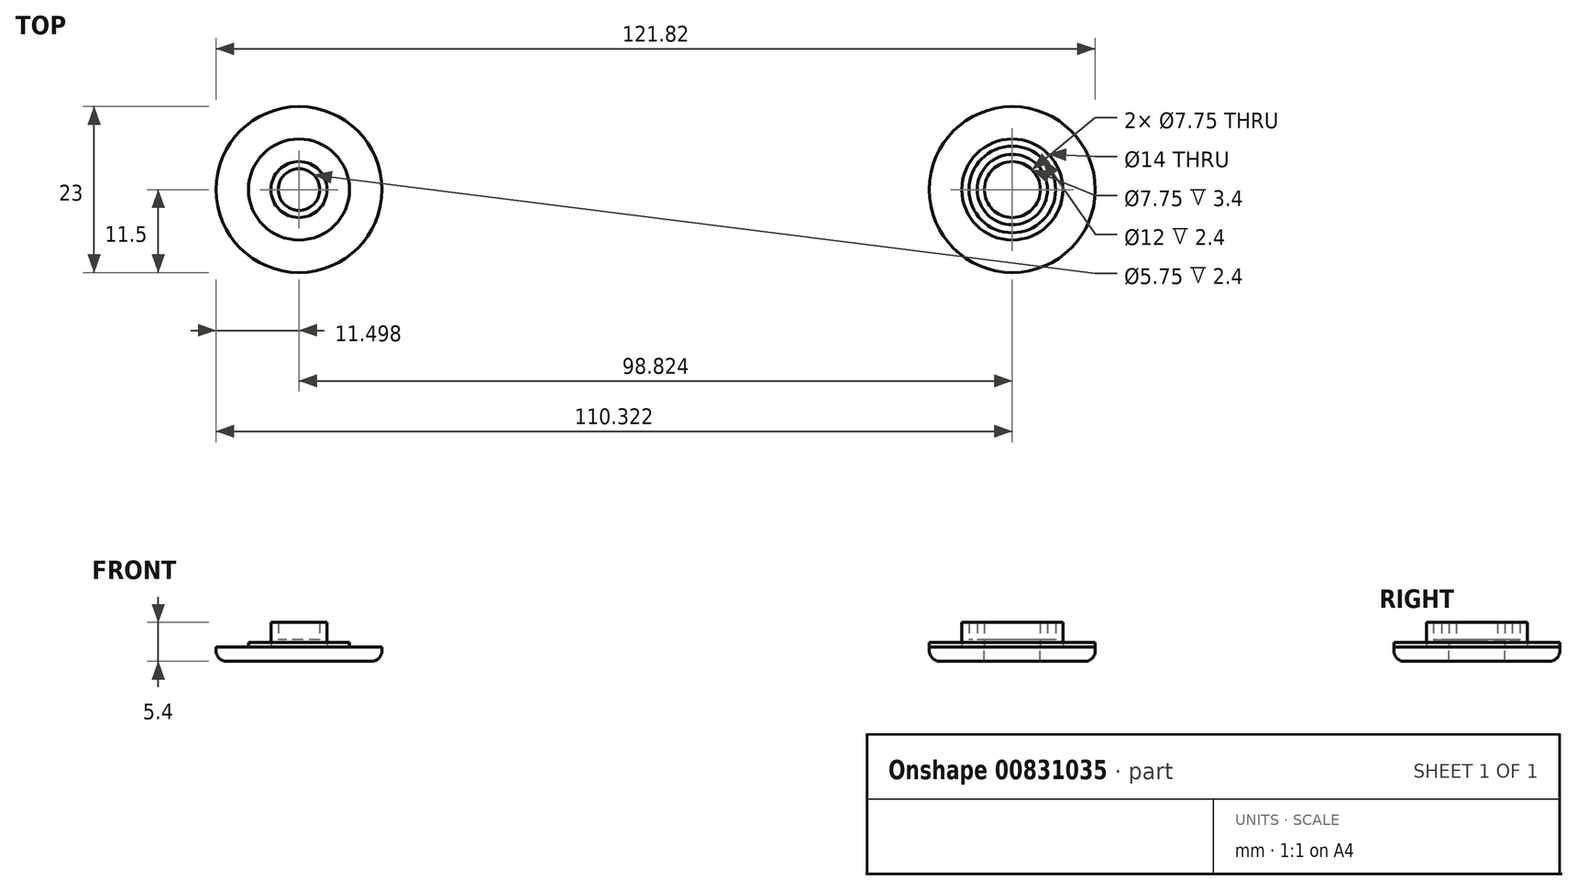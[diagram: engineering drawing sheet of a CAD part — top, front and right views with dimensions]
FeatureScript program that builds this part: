
annotation { "Feature Type Name" : "Feature", "Feature Type Description" : "" }
export const myFeature = defineFeature(function(context is Context, id is Id, definition is map)
    precondition{}
    {
        {
            var Q0;
            Q0=qCreatedBy(makeId("Top.planeOp"),FACE);
            var sketch = newSketch(context, id + "F0", { "sketchPlane" : qUnion([Q0])});
            skCircle(sketch, "E0", {"center": v(-49.41, 0) * mm, "radius": 3.88 * mm});
            skCircle(sketch, "E1", {"center": v(-49.41, 0) * mm, "radius": 7 * mm});
            skCircle(sketch, "E2", {"center": v(-49.41, 0) * mm, "radius": 11.5 * mm});
            skCircle(sketch, "E3.MirrorC", {"center": v(49.41, 0) * mm, "radius": 11.5 * mm});
            skCircle(sketch, "E4.MirrorC", {"center": v(49.41, 0) * mm, "radius": 7 * mm});
            skCircle(sketch, "E5.MirrorC", {"center": v(49.41, 0) * mm, "radius": 3.88 * mm});
            skSolve(sketch);
        }
        {
            var Q0;
            Q0=makeQuery(id+"F0.imprint","IMPRINT",FACE,{"disambiguationData":[TD([[makeQuery(id+"F0.imprint","IMPRINT",EDGE,{"derivedFrom":sQuery(id+"F0.wireOp",EDGE,"E0")}),1.0]])]});
            var Q1;
            Q1=makeQuery(id+"F0.imprint","IMPRINT",FACE,{"disambiguationData":[TD([[makeQuery(id+"F0.imprint","IMPRINT",EDGE,{"derivedFrom":sQuery(id+"F0.wireOp",EDGE,"E5.MirrorC")}),-1.0]])]});
            extrude(context, id + "F1", {"entities" : qUnion([Q0, Q1]), "depth" : 3.4 * mm, "offsetDistance" : 25 * mm});
        }
        {
            var Q0;
            Q0=makeQuery(id+"F0.imprint","IMPRINT",FACE,{"disambiguationData":[TD([[makeQuery(id+"F0.imprint","IMPRINT",EDGE,{"derivedFrom":sQuery(id+"F0.wireOp",EDGE,"E0")}),-1.0]])]});
            var Q1;
            Q1=makeQuery(id+"F0.imprint","IMPRINT",FACE,{"disambiguationData":[TD([[makeQuery(id+"F0.imprint","IMPRINT",EDGE,{"derivedFrom":sQuery(id+"F0.wireOp",EDGE,"E4.MirrorC")}),-1.0]])]});
            extrude(context, id + "F2", {"entities" : qUnion([Q0, Q1]), "depth" : 0.6 * mm, "offsetDistance" : 25 * mm});
        }
        {
            var Q0;
            Q0=makeQuery(id+"F0.imprint","IMPRINT",FACE,{"disambiguationData":[TD([[makeQuery(id+"F0.imprint","IMPRINT",EDGE,{"derivedFrom":sQuery(id+"F0.wireOp",EDGE,"E1")}),-1.0]])]});
            var Q1;
            Q1=makeQuery(id+"F0.imprint","IMPRINT",FACE,{"disambiguationData":[TD([[makeQuery(id+"F0.imprint","IMPRINT",EDGE,{"derivedFrom":sQuery(id+"F0.wireOp",EDGE,"E3.MirrorC")}),-1.0]])]});
            var Q2;
            Q2=makeQuery(id+"F0.imprint","IMPRINT",FACE,{"disambiguationData":[TD([[makeQuery(id+"F0.imprint","IMPRINT",EDGE,{"derivedFrom":sQuery(id+"F0.wireOp",EDGE,"E0")}),-1.0]])]});
            var Q3;
            Q3=makeQuery(id+"F0.imprint","IMPRINT",FACE,{"disambiguationData":[TD([[makeQuery(id+"F0.imprint","IMPRINT",EDGE,{"derivedFrom":sQuery(id+"F0.wireOp",EDGE,"E0")}),1.0]])]});
            var Q4;
            Q4=makeQuery(id+"F0.imprint","IMPRINT",FACE,{"disambiguationData":[TD([[makeQuery(id+"F0.imprint","IMPRINT",EDGE,{"derivedFrom":sQuery(id+"F0.wireOp",EDGE,"E5.MirrorC")}),-1.0]])]});
            var Q5;
            Q5=makeQuery(id+"F0.imprint","IMPRINT",FACE,{"disambiguationData":[TD([[makeQuery(id+"F0.imprint","IMPRINT",EDGE,{"derivedFrom":sQuery(id+"F0.wireOp",EDGE,"E4.MirrorC")}),-1.0]])]});
            extrude(context, id + "F3", {"entities" : qUnion([Q0, Q1, Q2, Q3, Q4, Q5]), "oppositeDirection" : true, "depth" : 2 * mm, "offsetDistance" : 25 * mm});
        }
        {
            var Q0;
            Q0=makeQuery(id+"F1.opExtrude","CAP_FACE",FACE,{"disambiguationData":[OSD([sQuery(id+"F0.wireOp",EDGE,"E0")])],"isStart":false});
            var Q1;
            Q1=makeQuery(id+"F1.opExtrude","CAP_FACE",FACE,{"disambiguationData":[OSD([sQuery(id+"F0.wireOp",EDGE,"E5.MirrorC")])],"isStart":false});
            shell(context, id + "F4", {"entities" : qUnion([Q0, Q1]), "thickness" : 1 * mm});
        }
        {
            var Q0;
            Q0=makeQuery(id+"F3.opExtrude","CAP_EDGE",EDGE,{"disambiguationData":[OSD([sQuery(id+"F0.wireOp",EDGE,"E3.MirrorC")])],"isStart":false});
            var Q1;
            Q1=makeQuery(id+"F3.opExtrude","CAP_EDGE",EDGE,{"disambiguationData":[OSD([sQuery(id+"F0.wireOp",EDGE,"E2")])],"isStart":false});
            fillet(context, id + "F5", {"entities" : qUnion([Q0, Q1]), "radius" : 1.5 * mm, "tangentPropagation" : true, "allowEdgeOverflow" : false});
        }
    });
